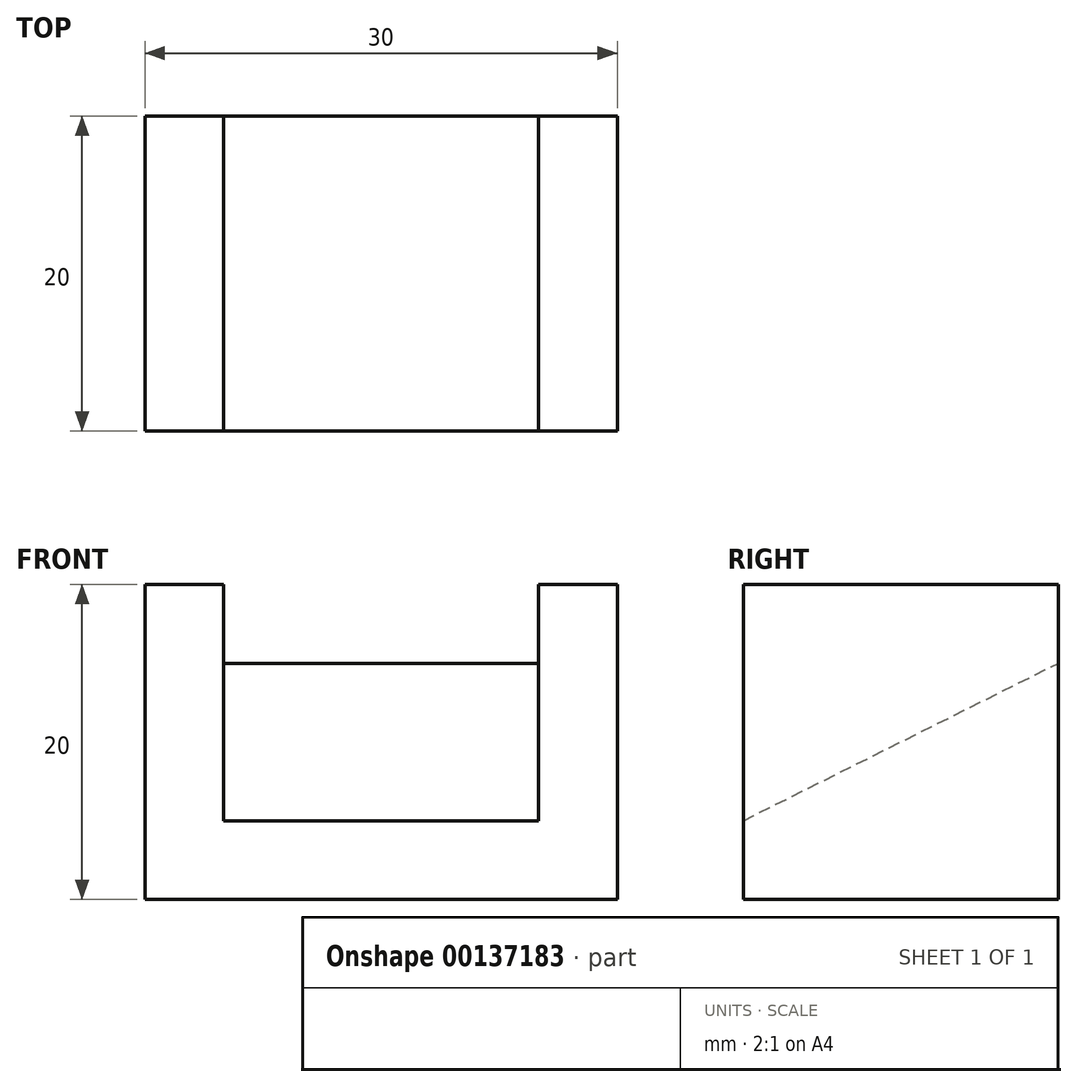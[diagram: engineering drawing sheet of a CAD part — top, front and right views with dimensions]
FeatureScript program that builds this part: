
annotation { "Feature Type Name" : "Feature", "Feature Type Description" : "" }
export const myFeature = defineFeature(function(context is Context, id is Id, definition is map)
    precondition{}
    {
        {
            var Q0;
            Q0=qCreatedBy(makeId("Right.planeOp"),FACE);
            var sketch = newSketch(context, id + "F0", { "sketchPlane" : qUnion([Q0])});
            skLineSegment(sketch, "E0", {"start": v(0, 0) * mm, "end": v(20, 10) * mm});
            skLineSegment(sketch, "E1", {"start": v(20, 10) * mm, "end": v(20, 0) * mm});
            skLineSegment(sketch, "E2", {"start": v(20, 0) * mm, "end": v(0, 0) * mm});
            skSolve(sketch);
        }
        {
            var Q0;
            Q0 = qSketchRegion(id + "F0", true);
            extrude(context, id + "F1", {"entities" : qUnion([Q0]), "depth" : 20 * mm});
        }
        {
            var Q0;
            Q0=qCreatedBy(makeId("Front.planeOp"),FACE);
            var sketch = newSketch(context, id + "F2", { "sketchPlane" : qUnion([Q0])});
            skLineSegment(sketch, "E3", {"start": v(0, 15) * mm, "end": v(0, 0) * mm});
            skLineSegment(sketch, "E4", {"start": v(0, 0) * mm, "end": v(20, 0) * mm});
            skLineSegment(sketch, "E5", {"start": v(20, 0) * mm, "end": v(20, 15) * mm});
            skLineSegment(sketch, "E6", {"start": v(20, 15) * mm, "end": v(25, 15) * mm});
            skLineSegment(sketch, "E7", {"start": v(25, 15) * mm, "end": v(25, -5) * mm});
            skLineSegment(sketch, "E8", {"start": v(25, -5) * mm, "end": v(-5, -5) * mm});
            skLineSegment(sketch, "E9", {"start": v(-5, -5) * mm, "end": v(-5, 15) * mm});
            skLineSegment(sketch, "E10", {"start": v(-5, 15) * mm, "end": v(0, 15) * mm});
            skSolve(sketch);
        }
        {
            var Q0;
            Q0 = qSketchRegion(id + "F2", true);
            extrude(context, id + "F3", {"entities" : qUnion([Q0]), "operationType" : NewBodyOperationType.ADD, "oppositeDirection" : true, "depth" : 20 * mm});
        }
    });
